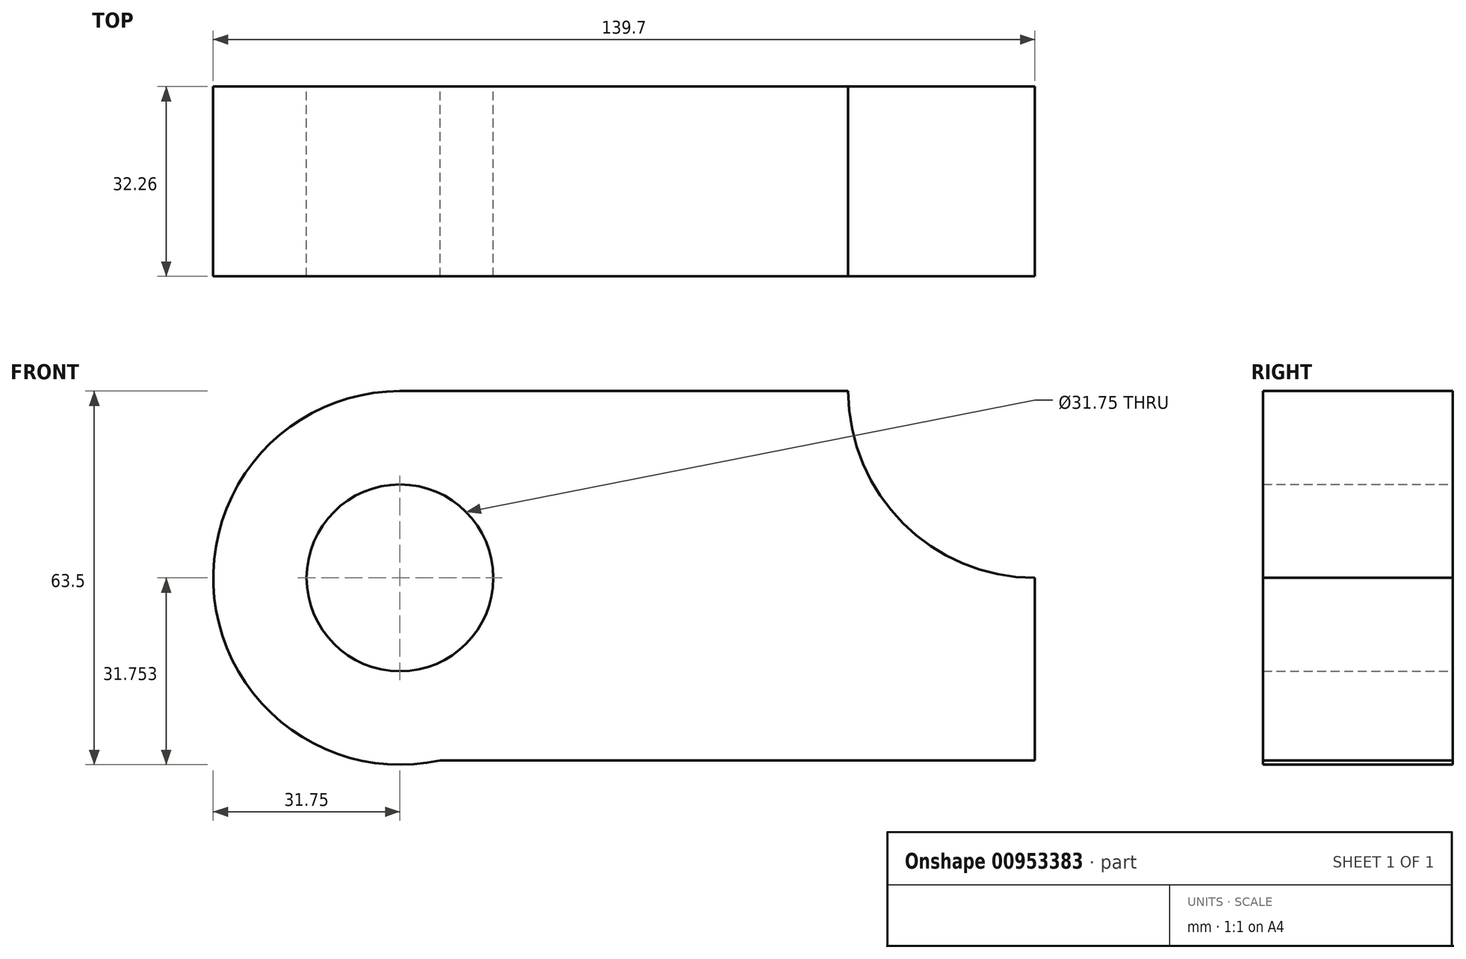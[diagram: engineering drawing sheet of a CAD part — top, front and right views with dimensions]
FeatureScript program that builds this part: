
annotation { "Feature Type Name" : "Feature", "Feature Type Description" : "" }
export const myFeature = defineFeature(function(context is Context, id is Id, definition is map)
    precondition{}
    {
        {
            var Q0;
            Q0=qCreatedBy(makeId("Front.planeOp"),FACE);
            var sketch = newSketch(context, id + "F0", { "sketchPlane" : qUnion([Q0])});
            skCircle(sketch, "E0", {"center": v(0, 31.01) * mm, "radius": 15.88 * mm});
            skCircle(sketch, "E1", {"center": v(0, 31.01) * mm, "radius": 31.75 * mm});
            skLineSegment(sketch, "E2.bottom", {"start": v(0, 62.76) * mm, "end": v(76.2, 62.76) * mm});
            skLineSegment(sketch, "E2.top", {"start": v(0, 0) * mm, "end": v(107.95, 0) * mm});
            skLineSegment(sketch, "E2.left", {"start": v(0, 62.76) * mm, "end": v(0, 0) * mm});
            skLineSegment(sketch, "E2.right", {"start": v(107.95, 31.01) * mm, "end": v(107.95, 0) * mm});
            skArc(sketch, "E3", {"start": v(76.2, 62.76) * mm, "mid": v(85.5, 40.31) * mm, "end": v(107.95, 31.01) * mm});
            skSolve(sketch);
        }
        {
            var Q0;
            {var subQ0=sQuery(id+"F0.wireOp",EDGE,"E2.left");var subQ3=sQuery(id+"F0.wireOp",EDGE,"E0");var subQ4=makeQuery(id+"F0.imprint","INTERSECT",VERTEX,{"disambiguationData":[OD(0.0)],"derivedFrom":[subQ3,subQ0]});Q0=makeQuery(id+"F0.imprint","IMPRINT",FACE,{"disambiguationData":[TD([[makeQuery(id+"F0.imprint","IMPRINT",EDGE,{"disambiguationData":[TD([[subQ4,-1.0]])],"derivedFrom":subQ3}),-1.0]])]});}
            var Q1;
            {var subQ0=sQuery(id+"F0.wireOp",EDGE,"E2.left");var subQ3=sQuery(id+"F0.wireOp",EDGE,"E0");var subQ4=makeQuery(id+"F0.imprint","INTERSECT",VERTEX,{"disambiguationData":[OD(0.0)],"derivedFrom":[subQ3,subQ0]});Q1=makeQuery(id+"F0.imprint","IMPRINT",FACE,{"disambiguationData":[TD([[makeQuery(id+"F0.imprint","IMPRINT",EDGE,{"disambiguationData":[TD([[subQ4,1.0]])],"derivedFrom":subQ3}),-1.0]])]});}
            var Q2;
            {var subQ4=sQuery(id+"F0.wireOp",EDGE,"E2.bottom");Q2=makeQuery(id+"F0.imprint","IMPRINT",FACE,{"disambiguationData":[TD([[makeQuery(id+"F0.imprint","IMPRINT",EDGE,{"derivedFrom":subQ4}),-1.0]])]});}
            extrude(context, id + "F1", {"entities" : qUnion([Q0, Q1, Q2]), "depth" : 32.26 * mm, "offsetDistance" : 25.4 * mm});
        }
    });
